# Revit family: Accessory-Touchless-Soap_Dispenser-KOHLER-Composed-K-22848_1
name_source: partatom
category: Specialty Equipment
revit_build: Autodesk Revit 2017 (Build: 20160225_1515(x64)
units: mm (PartAtom-declared; Revit-internal decimal feet)

## family parameters
Cut with Voids When Loaded = No
Host = Face
OmniClass Number = 23.31.25.29.13
OmniClass Title = Hand Soap Dispensers
Part Type = Normal
Room Calculation Point = No
Round Connector Dimension = Use Diameter
Shared = No

## types (3) — shared parameters
ADA Compliant = No
Apparent Load = 0 VA
Assembly Code = C1030200
Date Modified = 08/17/2020
Default Elevation = 42"
Description = Wall Mount Foam Soap Dispenser-AC
Electrical Connector = Yes
Electrical Note = One Dedicated Circuit Required, Protected With Class A Ground-Fault Circuit-Interrupter (GFCI). Outside North America,
This Device May Be Known As a Residual Current Device (RCD).
Height = 1 5/8"
Length = 5 9/16"
Manufacturer = KOHLER Co.
Master Format 2014 = 10 28 00
Master Format 2014 Name = Toilet, Bath, and Laundry Accessories
Material = Cast Brass Construction
Product Documentation Link = https://www.us.kohler.com
Product Name = Composed
Product Page URL = http://www.us.kohler.com
URL = https://www.us.kohler.com
Voltage = 0 V
WaterSense Certified = No
Width = 1 5/8"

## per-type parameters (varying)
| type | Finish | Model | Type |
| CP-Polished Chrome | Kohler-Metal-CP-Polished_Chrome | K-22848-CP | 1 |
| BN-Vibrant Brushed Nickel | Kohler-Metal-BN-Vibrant_Brushed_Nickel | K-22848-BN | 2 |
| BL-Matte Black | Kohler-Metal-BL-Matte_Black | K-22848-BL | 3 |

## geometry (parser evidence)
native form markers: Sweep x4
no freeform markers — native parametric forms only
